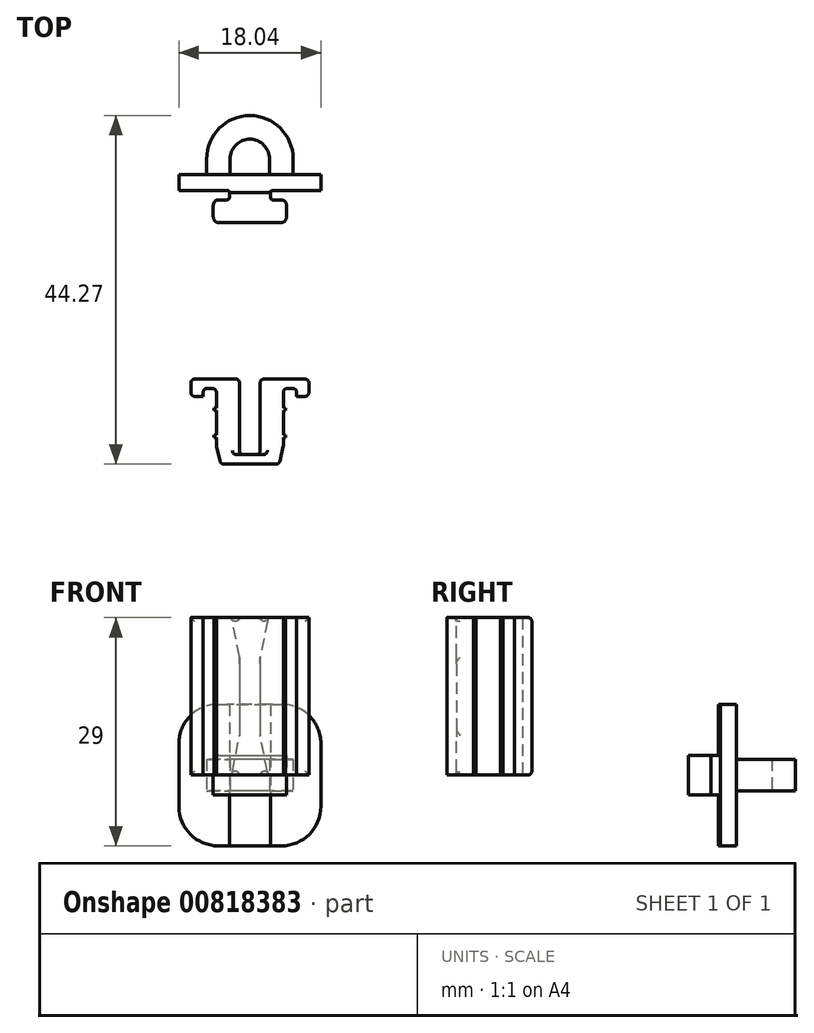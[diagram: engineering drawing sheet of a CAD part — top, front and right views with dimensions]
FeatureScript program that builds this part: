
annotation { "Feature Type Name" : "Feature", "Feature Type Description" : "" }
export const myFeature = defineFeature(function(context is Context, id is Id, definition is map)
    precondition{}
    {
        {
            var Q0;
            Q0=qCreatedBy(makeId("Top.planeOp"),FACE);
            var sketch = newSketch(context, id + "F0", { "sketchPlane" : qUnion([Q0])});
            skLineSegment(sketch, "E0", {"start": v(-3.7, 0) * mm, "end": v(3.7, 0) * mm});
            skLineSegment(sketch, "E1", {"start": v(4.25, 2.31) * mm, "end": v(4.25, 3.4) * mm});
            skLineSegment(sketch, "E2", {"start": v(4.25, 9.6) * mm, "end": v(5.95, 9.6) * mm});
            skLineSegment(sketch, "E3", {"start": v(5.95, 9.6) * mm, "end": v(5.95, 8.6) * mm});
            skLineSegment(sketch, "E4", {"start": v(5.95, 8.6) * mm, "end": v(7.5, 8.6) * mm});
            skLineSegment(sketch, "E5", {"start": v(7.5, 8.6) * mm, "end": v(7.5, 10.8) * mm});
            skLineSegment(sketch, "E6", {"start": v(7.5, 10.8) * mm, "end": v(1.3, 10.8) * mm});
            skLineSegment(sketch, "E7", {"start": v(1.3, 10.8) * mm, "end": v(1.3, 1.2) * mm});
            skLineSegment(sketch, "E8", {"start": v(1.3, 1.2) * mm, "end": v(-1.3, 1.2) * mm});
            skLineSegment(sketch, "E9", {"start": v(-1.3, 1.2) * mm, "end": v(-1.3, 10.8) * mm});
            skLineSegment(sketch, "E10", {"start": v(-1.3, 10.8) * mm, "end": v(-7.5, 10.8) * mm});
            skLineSegment(sketch, "E11", {"start": v(-7.5, 8.6) * mm, "end": v(-5.95, 8.6) * mm});
            skLineSegment(sketch, "E12", {"start": v(-5.95, 8.6) * mm, "end": v(-5.95, 9.6) * mm});
            skLineSegment(sketch, "E13", {"start": v(-5.95, 9.6) * mm, "end": v(-4.25, 9.6) * mm});
            skLineSegment(sketch, "E14", {"start": v(-4.25, 9.6) * mm, "end": v(-4.25, 7.1) * mm});
            skLineSegment(sketch, "E15", {"start": v(-7.5, 10.8) * mm, "end": v(-7.5, 8.6) * mm});
            skLineSegment(sketch, "E16", {"start": v(4.25, 7.1) * mm, "end": v(4.55, 7.1) * mm});
            skLineSegment(sketch, "E17", {"start": v(4.55, 7.1) * mm, "end": v(4.55, 6.8) * mm});
            skLineSegment(sketch, "E18", {"start": v(4.55, 6.8) * mm, "end": v(4.25, 6.8) * mm});
            skLineSegment(sketch, "E19", {"start": v(-4.25, 7.1) * mm, "end": v(-4.55, 7.1) * mm});
            skLineSegment(sketch, "E20", {"start": v(-4.55, 7.1) * mm, "end": v(-4.55, 6.8) * mm});
            skLineSegment(sketch, "E21", {"start": v(-4.55, 6.8) * mm, "end": v(-4.25, 6.8) * mm});
            skLineSegment(sketch, "E22", {"start": v(4.25, 3.7) * mm, "end": v(4.55, 3.7) * mm});
            skLineSegment(sketch, "E23", {"start": v(4.55, 3.7) * mm, "end": v(4.55, 3.4) * mm});
            skLineSegment(sketch, "E24", {"start": v(4.55, 3.4) * mm, "end": v(4.25, 3.4) * mm});
            skLineSegment(sketch, "E25", {"start": v(-4.25, 3.7) * mm, "end": v(-4.55, 3.7) * mm});
            skLineSegment(sketch, "E26", {"start": v(-4.55, 3.7) * mm, "end": v(-4.55, 3.4) * mm});
            skLineSegment(sketch, "E27", {"start": v(-4.55, 3.4) * mm, "end": v(-4.25, 3.4) * mm});
            skLineSegment(sketch, "E28", {"start": v(4.25, 2.31) * mm, "end": v(3.7, 0) * mm});
            skLineSegment(sketch, "E29", {"start": v(-4.25, 2.31) * mm, "end": v(-3.7, 0) * mm});
            skLineSegment(sketch, "E30.trimOffspring", {"start": v(4.25, 7.1) * mm, "end": v(4.25, 9.6) * mm});
            skLineSegment(sketch, "E31.trimOffspring", {"start": v(4.25, 3.7) * mm, "end": v(4.25, 6.8) * mm});
            skLineSegment(sketch, "E32.trimOffspring", {"start": v(-4.25, 6.8) * mm, "end": v(-4.25, 3.7) * mm});
            skLineSegment(sketch, "E33.trimOffspring", {"start": v(-4.25, 3.4) * mm, "end": v(-4.25, 2.31) * mm});
            skPoint(sketch, "E34.orphan", {"position": v(-4.25, 0) * mm});
            skSolve(sketch);
        }
        {
            var Q0;
            {var subQ0=sQuery(id+"F0.wireOp",EDGE,"E19");Q0=makeQuery(id+"F0.imprint","IMPRINT",FACE,{"disambiguationData":[TD([[makeQuery(id+"F0.imprint","IMPRINT",EDGE,{"derivedFrom":subQ0}),1.0]])]});}
            var Q1;
            {var subQ0=sQuery(id+"F0.wireOp",EDGE,"E25");Q1=makeQuery(id+"F0.imprint","IMPRINT",FACE,{"disambiguationData":[TD([[makeQuery(id+"F0.imprint","IMPRINT",EDGE,{"derivedFrom":subQ0}),1.0]])]});}
            var Q2;
            {var subQ10=sQuery(id+"F0.wireOp",EDGE,"E0");Q2=makeQuery(id+"F0.imprint","IMPRINT",FACE,{"disambiguationData":[TD([[makeQuery(id+"F0.imprint","IMPRINT",EDGE,{"derivedFrom":subQ10}),1.0]])]});}
            var Q3;
            {var subQ0=sQuery(id+"F0.wireOp",EDGE,"E16");Q3=makeQuery(id+"F0.imprint","IMPRINT",FACE,{"disambiguationData":[TD([[makeQuery(id+"F0.imprint","IMPRINT",EDGE,{"derivedFrom":subQ0}),-1.0]])]});}
            var Q4;
            {var subQ0=sQuery(id+"F0.wireOp",EDGE,"E22");Q4=makeQuery(id+"F0.imprint","IMPRINT",FACE,{"disambiguationData":[TD([[makeQuery(id+"F0.imprint","IMPRINT",EDGE,{"derivedFrom":subQ0}),-1.0]])]});}
            extrude(context, id + "F1", {"entities" : qUnion([Q0, Q1, Q2, Q3, Q4]), "depth" : 20 * mm, "offsetDistance" : 25 * mm});
        }
        {
            var Q0;
            Q0=makeQuery(id+"F1.opExtrude","SWEPT_FACE",FACE,{"disambiguationData":[OSD([sQuery(id+"F0.wireOp",EDGE,"E6")])]});
            var sketch = newSketch(context, id + "F2", { "sketchPlane" : qUnion([Q0])});
            skLineSegment(sketch, "E35.0", {"start": v(1.3, 20) * mm, "end": v(1.3, 0) * mm});
            skLineSegment(sketch, "E36", {"start": v(1.3, 0) * mm, "end": v(2.3, 0) * mm});
            skLineSegment(sketch, "E37", {"start": v(2.3, 0) * mm, "end": v(1.3, 5) * mm});
            skLineSegment(sketch, "E38", {"start": v(1.3, 5) * mm, "end": v(1.3, 15) * mm});
            skLineSegment(sketch, "E39.0", {"start": v(1.3, 20) * mm, "end": v(7.5, 20) * mm});
            skLineSegment(sketch, "E40", {"start": v(1.3, 15) * mm, "end": v(2.3, 20) * mm});
            skLineSegment(sketch, "E41", {"start": v(2.3, 20) * mm, "end": v(1.3, 20) * mm});
            skLineSegment(sketch, "E42", {"start": v(-1.3, 0) * mm, "end": v(-2.3, 0) * mm});
            skLineSegment(sketch, "E43", {"start": v(-2.3, 0) * mm, "end": v(-1.3, 5) * mm});
            skLineSegment(sketch, "E44", {"start": v(-1.3, 5) * mm, "end": v(-1.3, 0) * mm});
            skLineSegment(sketch, "E45", {"start": v(-1.3, 20) * mm, "end": v(-2.3, 20) * mm});
            skLineSegment(sketch, "E46", {"start": v(-2.3, 20) * mm, "end": v(-1.3, 15) * mm});
            skLineSegment(sketch, "E47", {"start": v(14.13, 10) * mm, "end": v(-21.24, 10) * mm, "construction": true});
            skPoint(sketch, "E47.startSnap0", {"position": v(1.3, 10) * mm});
            skPoint(sketch, "E47.endSnap0", {"position": v(-7.5, 10) * mm});
            skSolve(sketch);
        }
        {
            var Q0;
            {var subQ0=sQuery(id+"F2.wireOp",EDGE,"E36");Q0=makeQuery(id+"F2.imprint","IMPRINT",FACE,{"disambiguationData":[TD([[makeQuery(id+"F2.imprint","IMPRINT",EDGE,{"derivedFrom":subQ0}),1.0]])]});}
            var Q1;
            Q1=makeQuery(id+"F2.imprint","IMPRINT",FACE,{"disambiguationData":[TD([[makeQuery(id+"F2.imprint","IMPRINT",EDGE,{"derivedFrom":sQuery(id+"F2.wireOp",EDGE,"E42")}),1.0]])]});
            var Q2;
            {var subQ0=sQuery(id+"F2.wireOp",EDGE,"E45");Q2=makeQuery(id+"F2.imprint","IMPRINT",FACE,{"disambiguationData":[TD([[makeQuery(id+"F2.imprint","IMPRINT",EDGE,{"derivedFrom":subQ0}),-1.0]])]});}
            var Q3;
            {var subQ2=sQuery(id+"F2.wireOp",EDGE,"E40");Q3=makeQuery(id+"F2.imprint","IMPRINT",FACE,{"disambiguationData":[TD([[makeQuery(id+"F2.imprint","IMPRINT",EDGE,{"derivedFrom":subQ2}),1.0]])]});}
            extrude(context, id + "F3", {"entities" : qUnion([Q0, Q1, Q2, Q3]), "operationType" : NewBodyOperationType.REMOVE, "oppositeDirection" : true, "depth" : 9.6 * mm, "offsetDistance" : 25 * mm});
        }
        {
            var Q0;
            Q0=makeQuery(id+"F1.opExtrude","SWEPT_FACE",FACE,{"disambiguationData":[OSD([sQuery(id+"F0.wireOp",EDGE,"E6")])]});
            var Q1;
            Q1=makeQuery(id+"F1.opExtrude","SWEPT_FACE",FACE,{"disambiguationData":[OSD([sQuery(id+"F0.wireOp",EDGE,"E10")])]});
            var Q2;
            Q2=makeQuery(id+"F3.boolean.opBoolean","COPY",FACE,{"derivedFrom":makeQuery(id+"F3.opExtrude","SWEPT_FACE",FACE,{"disambiguationData":[OSD([sQuery(id+"F2.wireOp",EDGE,"E37")])]})});
            var Q3;
            Q3=makeQuery(id+"F3.boolean.opBoolean","COPY",FACE,{"derivedFrom":makeQuery(id+"F3.opExtrude","SWEPT_FACE",FACE,{"disambiguationData":[OSD([sQuery(id+"F2.wireOp",EDGE,"E43")])]})});
            var Q4;
            Q4=makeQuery(id+"F3.boolean.opBoolean","COPY",FACE,{"derivedFrom":makeQuery(id+"F3.opExtrude","SWEPT_FACE",FACE,{"disambiguationData":[OSD([sQuery(id+"F2.wireOp",EDGE,"E46")])]})});
            var Q5;
            Q5=makeQuery(id+"F3.boolean.opBoolean","COPY",FACE,{"derivedFrom":makeQuery(id+"F3.opExtrude","SWEPT_FACE",FACE,{"disambiguationData":[OSD([sQuery(id+"F2.wireOp",EDGE,"E40")])]})});
            var Q6;
            Q6=makeQuery(id+"F1.opExtrude","SWEPT_EDGE",EDGE,{"disambiguationData":[OSD([sQuery(id+"F0.wireOp",EDGE,"E13"),sQuery(id+"F0.wireOp",EDGE,"E14")])]});
            var Q7;
            Q7=makeQuery(id+"F1.opExtrude","SWEPT_EDGE",EDGE,{"disambiguationData":[OSD([sQuery(id+"F0.wireOp",EDGE,"E12"),sQuery(id+"F0.wireOp",EDGE,"E13")])]});
            var Q8;
            Q8=makeQuery(id+"F1.opExtrude","SWEPT_EDGE",EDGE,{"disambiguationData":[OSD([sQuery(id+"F0.wireOp",EDGE,"E2"),sQuery(id+"F0.wireOp",EDGE,"E30.trimOffspring")])]});
            var Q9;
            Q9=makeQuery(id+"F1.opExtrude","SWEPT_EDGE",EDGE,{"disambiguationData":[OSD([sQuery(id+"F0.wireOp",EDGE,"E2"),sQuery(id+"F0.wireOp",EDGE,"E3")])]});
            var Q10;
            Q10=makeQuery(id+"F1.opExtrude","SWEPT_EDGE",EDGE,{"disambiguationData":[OSD([sQuery(id+"F0.wireOp",EDGE,"E11"),sQuery(id+"F0.wireOp",EDGE,"E15")])]});
            var Q11;
            Q11=makeQuery(id+"F1.opExtrude","SWEPT_EDGE",EDGE,{"disambiguationData":[OSD([sQuery(id+"F0.wireOp",EDGE,"E4"),sQuery(id+"F0.wireOp",EDGE,"E5")])]});
            var Q12;
            Q12=makeQuery(id+"F1.opExtrude","SWEPT_EDGE",EDGE,{"disambiguationData":[OSD([sQuery(id+"F0.wireOp",EDGE,"E0"),sQuery(id+"F0.wireOp",EDGE,"E28")])]});
            var Q13;
            Q13=makeQuery(id+"F1.opExtrude","SWEPT_EDGE",EDGE,{"disambiguationData":[OSD([sQuery(id+"F0.wireOp",EDGE,"E1"),sQuery(id+"F0.wireOp",EDGE,"E28")])]});
            var Q14;
            Q14=makeQuery(id+"F1.opExtrude","SWEPT_EDGE",EDGE,{"disambiguationData":[OSD([sQuery(id+"F0.wireOp",EDGE,"E29"),sQuery(id+"F0.wireOp",EDGE,"E33.trimOffspring")])]});
            var Q15;
            Q15=makeQuery(id+"F1.opExtrude","SWEPT_EDGE",EDGE,{"disambiguationData":[OSD([sQuery(id+"F0.wireOp",EDGE,"E0"),sQuery(id+"F0.wireOp",EDGE,"E29")])]});
            fillet(context, id + "F4", {"entities" : qUnion([Q0, Q1, Q2, Q3, Q4, Q5, Q6, Q7, Q8, Q9, Q10, Q11, Q12, Q13, Q14, Q15]), "radius" : 0.5 * mm, "tangentPropagation" : true, "allowEdgeOverflow" : false});
        }
        {
            var Q0;
            Q0=qCreatedBy(makeId("Top.planeOp"),FACE);
            var sketch = newSketch(context, id + "F5", { "sketchPlane" : qUnion([Q0])});
            skLineSegment(sketch, "E48.bottom", {"start": v(-3.95, 33.57) * mm, "end": v(-2.9, 33.57) * mm});
            skLineSegment(sketch, "E48.top", {"start": v(-3.95, 30.67) * mm, "end": v(3.95, 30.67) * mm});
            skLineSegment(sketch, "E48.left", {"start": v(-4.65, 32.87) * mm, "end": v(-4.65, 31.37) * mm});
            skLineSegment(sketch, "E48.right", {"start": v(4.65, 32.87) * mm, "end": v(4.65, 31.37) * mm});
            skLineSegment(sketch, "E49.left", {"start": v(-2.6, 33.87) * mm, "end": v(-2.6, 34.47) * mm});
            skLineSegment(sketch, "E49.right", {"start": v(2.6, 33.87) * mm, "end": v(2.6, 34.47) * mm});
            skLineSegment(sketch, "E50.bottom", {"start": v(-9.02, 34.77) * mm, "end": v(-2.9, 34.77) * mm});
            skLineSegment(sketch, "E50.top", {"start": v(-9.02, 36.77) * mm, "end": v(9.02, 36.77) * mm});
            skLineSegment(sketch, "E50.left", {"start": v(-9.02, 34.77) * mm, "end": v(-9.02, 36.77) * mm});
            skLineSegment(sketch, "E51.trimOffspring", {"start": v(2.9, 34.77) * mm, "end": v(9.02, 34.77) * mm});
            skLineSegment(sketch, "E52.trimOffspring", {"start": v(2.9, 33.57) * mm, "end": v(3.95, 33.57) * mm});
            skPoint(sketch, "E53.visualSharp", {"position": v(-2.6, 34.77) * mm});
            skArc(sketch, "E53.filletArc", {"start": v(-2.6, 34.47) * mm, "mid": v(-2.69, 34.68) * mm, "end": v(-2.9, 34.77) * mm});
            skPoint(sketch, "E54.visualSharp", {"position": v(2.6, 34.77) * mm});
            skArc(sketch, "E54.filletArc", {"start": v(2.9, 34.77) * mm, "mid": v(2.69, 34.68) * mm, "end": v(2.6, 34.47) * mm});
            skPoint(sketch, "E55.visualSharp", {"position": v(-2.6, 33.57) * mm});
            skArc(sketch, "E55.filletArc", {"start": v(-2.9, 33.57) * mm, "mid": v(-2.69, 33.66) * mm, "end": v(-2.6, 33.87) * mm});
            skPoint(sketch, "E56.visualSharp", {"position": v(2.6, 33.57) * mm});
            skArc(sketch, "E56.filletArc", {"start": v(2.6, 33.87) * mm, "mid": v(2.69, 33.66) * mm, "end": v(2.9, 33.57) * mm});
            skPoint(sketch, "E57.visualSharp", {"position": v(4.65, 33.57) * mm});
            skArc(sketch, "E57.filletArc", {"start": v(4.65, 32.87) * mm, "mid": v(4.44, 33.37) * mm, "end": v(3.95, 33.57) * mm});
            skPoint(sketch, "E58.visualSharp", {"position": v(4.65, 30.67) * mm});
            skPoint(sketch, "E59.visualSharp", {"position": v(-4.65, 30.67) * mm});
            skPoint(sketch, "E60.visualSharp", {"position": v(-4.65, 33.57) * mm});
            skArc(sketch, "E60.filletArc", {"start": v(-3.95, 33.57) * mm, "mid": v(-4.44, 33.37) * mm, "end": v(-4.65, 32.87) * mm});
            skLineSegment(sketch, "E61", {"start": v(-9.02, 34.77) * mm, "end": v(9.02, 34.77) * mm});
            skArc(sketch, "E62.filletArc", {"start": v(3.95, 30.67) * mm, "mid": v(4.44, 30.88) * mm, "end": v(4.65, 31.37) * mm});
            skArc(sketch, "E63.filletArc", {"start": v(-4.65, 31.37) * mm, "mid": v(-4.44, 30.88) * mm, "end": v(-3.95, 30.67) * mm});
            skLineSegment(sketch, "E64.bottom", {"start": v(2.75, 34.77) * mm, "end": v(-2.75, 34.77) * mm});
            skLineSegment(sketch, "E64.top", {"start": v(2.6, 34.47) * mm, "end": v(-2.6, 34.47) * mm});
            skLineSegment(sketch, "E65", {"start": v(9.02, 36.77) * mm, "end": v(9.02, 34.77) * mm});
            skPoint(sketch, "E66", {"position": v(0, 38.77) * mm});
            skLineSegment(sketch, "E67", {"start": v(2.5, 36.77) * mm, "end": v(2.5, 38.77) * mm});
            skLineSegment(sketch, "E68", {"start": v(5.5, 36.77) * mm, "end": v(5.5, 38.77) * mm});
            skLineSegment(sketch, "E69", {"start": v(-2.5, 36.77) * mm, "end": v(-2.5, 38.77) * mm});
            skLineSegment(sketch, "E70", {"start": v(-5.5, 36.77) * mm, "end": v(-5.5, 38.77) * mm});
            skArc(sketch, "E71", {"start": v(2.5, 38.77) * mm, "mid": v(0, 41.27) * mm, "end": v(-2.5, 38.77) * mm});
            skArc(sketch, "E72", {"start": v(5.5, 38.77) * mm, "mid": v(0, 44.27) * mm, "end": v(-5.5, 38.77) * mm});
            skSolve(sketch);
        }
        {
            var Q0;
            Q0=makeQuery(id+"F5.imprint","IMPRINT",FACE,{"disambiguationData":[TD([[makeQuery(id+"F5.imprint","IMPRINT",EDGE,{"derivedFrom":sQuery(id+"F5.wireOp",EDGE,"E48.bottom")}),-1.0]])]});
            var Q1;
            {var subQ1=sQuery(id+"F5.wireOp",EDGE,"E53.filletArc");Q1=makeQuery(id+"F5.imprint","IMPRINT",FACE,{"disambiguationData":[TD([[makeQuery(id+"F5.imprint","IMPRINT",EDGE,{"derivedFrom":subQ1}),-1.0]])]});}
            extrude(context, id + "F6", {"entities" : qUnion([Q0, Q1]), "endBound" : BoundingType.SYMMETRIC, "depth" : 5 * mm, "offsetDistance" : 25 * mm});
        }
        {
            var Q0;
            {var subQ3=sQuery(id+"F5.wireOp",EDGE,"E50.bottom");Q0=makeQuery(id+"F5.imprint","IMPRINT",FACE,{"disambiguationData":[TD([[makeQuery(id+"F5.imprint","IMPRINT",EDGE,{"derivedFrom":subQ3}),1.0]])]});}
            var Q1;
            {var subQ1=sQuery(id+"F5.wireOp",EDGE,"E53.filletArc");Q1=makeQuery(id+"F5.imprint","IMPRINT",FACE,{"disambiguationData":[TD([[makeQuery(id+"F5.imprint","IMPRINT",EDGE,{"derivedFrom":subQ1}),-1.0]])]});}
            extrude(context, id + "F7", {"entities" : qUnion([Q0, Q1]), "operationType" : NewBodyOperationType.ADD, "endBound" : BoundingType.SYMMETRIC, "depth" : 18 * mm, "offsetDistance" : 25 * mm, "hasSecondDirection" : true, "secondDirectionOppositeDirection" : true, "secondDirectionDepth" : (9 - 3.5) * mm});
        }
        {
            var Q0;
            {var subQ1=sQuery(id+"F5.wireOp",EDGE,"E67");Q0=makeQuery(id+"F5.imprint","IMPRINT",FACE,{"disambiguationData":[TD([[makeQuery(id+"F5.imprint","IMPRINT",EDGE,{"derivedFrom":subQ1}),-1.0]])]});}
            extrude(context, id + "F8", {"entities" : qUnion([Q0]), "operationType" : NewBodyOperationType.ADD, "endBound" : BoundingType.SYMMETRIC, "depth" : 4 * mm, "offsetDistance" : 25 * mm});
        }
        {
            var Q0;
            Q0=makeQuery(id+"F7.opExtrude","CAP_EDGE",EDGE,{"disambiguationData":[OSD([sQuery(id+"F5.wireOp",EDGE,"E50.right")])],"isStart":false});
            var Q1;
            Q1=makeQuery(id+"F7.opExtrude","CAP_EDGE",EDGE,{"disambiguationData":[OSD([sQuery(id+"F5.wireOp",EDGE,"E50.left")])],"isStart":false});
            var Q2;
            Q2=makeQuery(id+"F7.opExtrude","CAP_EDGE",EDGE,{"disambiguationData":[OSD([sQuery(id+"F5.wireOp",EDGE,"E50.right")])],"isStart":true});
            var Q3;
            Q3=makeQuery(id+"F7.opExtrude","CAP_EDGE",EDGE,{"disambiguationData":[OSD([sQuery(id+"F5.wireOp",EDGE,"E50.left")])],"isStart":true});
            var Q4;
            Q4=makeQuery(id+"F7.opExtrude","CAP_EDGE",EDGE,{"disambiguationData":[OSD([sQuery(id+"F5.wireOp",EDGE,"E65")])],"isStart":false});
            var Q5;
            Q5=makeQuery(id+"F7.opExtrude","CAP_EDGE",EDGE,{"disambiguationData":[OSD([sQuery(id+"F5.wireOp",EDGE,"E65")])],"isStart":true});
            fillet(context, id + "F9", {"entities" : qUnion([Q0, Q1, Q2, Q3, Q4, Q5]), "radius" : 5 * mm, "tangentPropagation" : true, "allowEdgeOverflow" : false});
        }
    });
